# Revit family: Haworth_BeHold_Accessory_SlimC-Cubby
name_source: partatom
category: Furniture Systems
revit_build: Autodesk Revit 2018 (Build: 20170223_1515(x64)
units: mm (PartAtom-declared; Revit-internal decimal feet)

## family parameters
Always vertical = Yes
Cut with Voids When Loaded = No
OmniClass Number = 23.40.70.14.64.21
OmniClass Title = Systems Furniture
Part Type = Normal
Room Calculation Point = No
Round Connector Dimension = Use Diameter
Shared = No
Work Plane-Based = No

## types (3) — shared parameters
Actual Depth = 12"
Actual Width = 10"
Assembly Code = E2020200
Custom Size = No
Description = Haworth - Be_Hold - Accessory - Slim C Cubby
Manufacturer = Haworth
Max. Depth = 12"
Max. Height = 15"
Max. Width = 10"
Min. Depth = 12"
Min. Height = 7"
Min. Width = 10"
Model = Haworth Be_Hold
Revision Number = 1
Size = Verify Final Dim. w/ Haworth
Standard Heights = 7, 13, 15 in.
Sustainability Info = https://www.haworth.com
Warranty = http://www.haworth.com

## per-type parameters (varying)
| type | Actual Height | Height | URL | URL - Product |
| 15h | 15" | 15" | http://www.haworth.com | http://www.haworth.com |
| 13h | 13" | 13" | www.haworth.com |  |
| 7h | 7" | 7" | www.haworth.com |  |

## geometry (parser evidence)
native form markers: Sweep x3
no freeform markers — native parametric forms only
